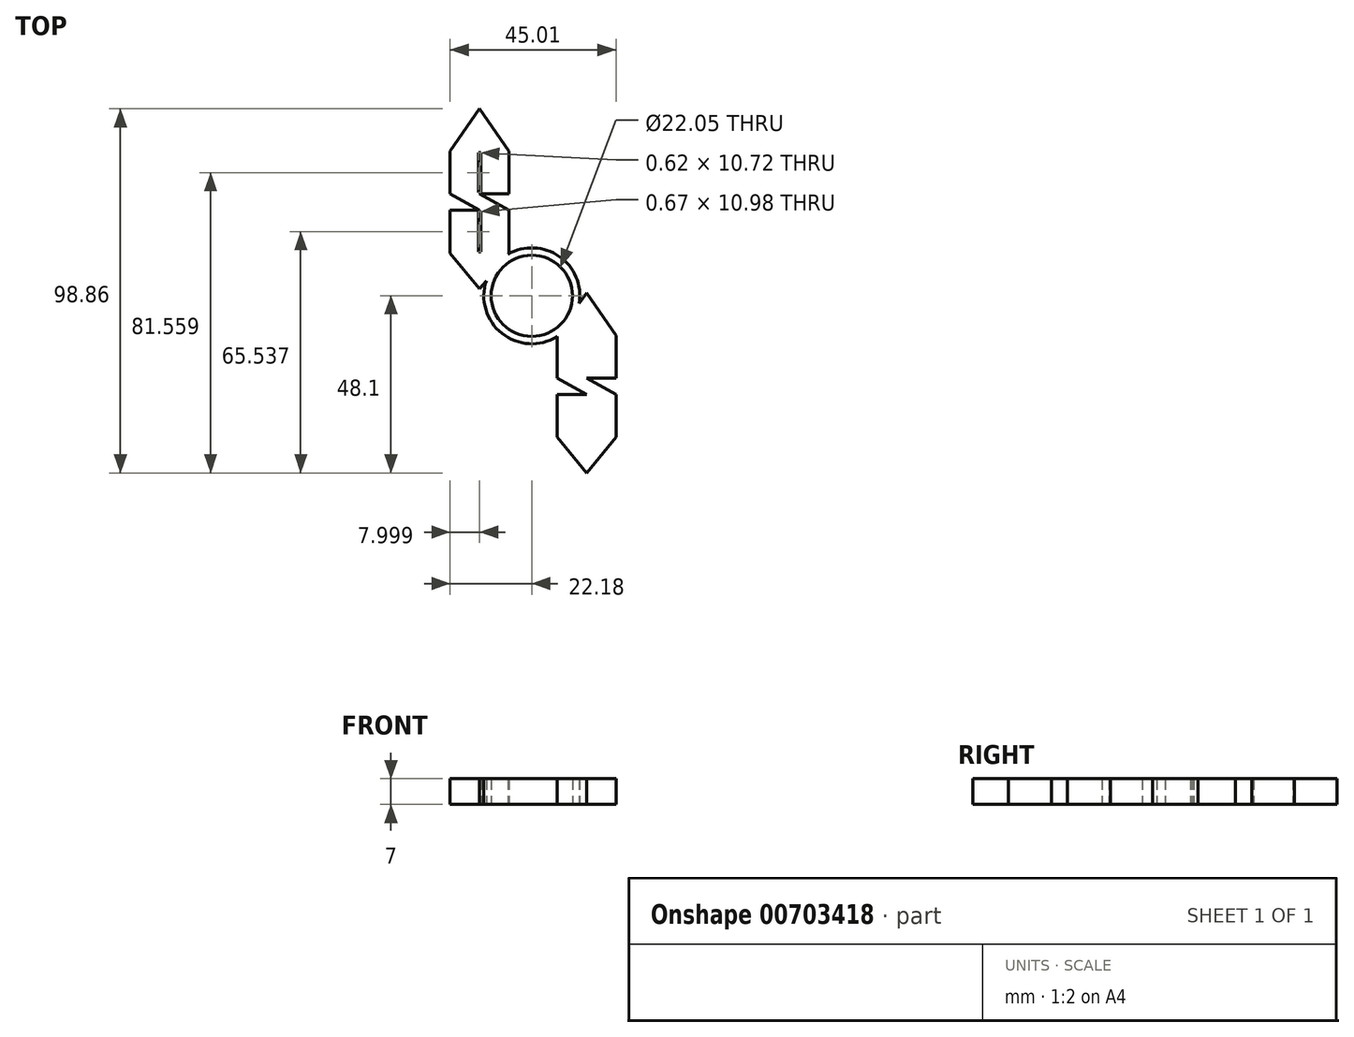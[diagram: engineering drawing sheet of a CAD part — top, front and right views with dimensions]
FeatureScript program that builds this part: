
annotation { "Feature Type Name" : "Feature", "Feature Type Description" : "" }
export const myFeature = defineFeature(function(context is Context, id is Id, definition is map)
    precondition{}
    {
        {
            var Q0;
            Q0=qCreatedBy(makeId("Top.planeOp"),FACE);
            var sketch = newSketch(context, id + "F0", { "sketchPlane" : qUnion([Q0])});
            skCircle(sketch, "E0", {"center": v(0, 0) * mm, "radius": 11.03 * mm});
            skCircle(sketch, "E1.0", {"center": v(0, 0) * mm, "radius": 13.02 * mm});
            skLineSegment(sketch, "E2", {"start": v(-6.18, 11.63) * mm, "end": v(-6.18, 23.25) * mm});
            skLineSegment(sketch, "E3", {"start": v(-14.18, 11.63) * mm, "end": v(-14.18, 23.25) * mm});
            skLineSegment(sketch, "E4", {"start": v(-22.18, 23.25) * mm, "end": v(-22.18, 11.63) * mm});
            skLineSegment(sketch, "E5", {"start": v(-6.18, 27.65) * mm, "end": v(-6.18, 39.27) * mm});
            skLineSegment(sketch, "E6", {"start": v(-14.18, 27.65) * mm, "end": v(-14.18, 39.27) * mm});
            skLineSegment(sketch, "E7", {"start": v(-22.18, 39.27) * mm, "end": v(-22.18, 27.65) * mm});
            skLineSegment(sketch, "E8", {"start": v(-6.18, 39.27) * mm, "end": v(-14.18, 50.76) * mm});
            skLineSegment(sketch, "E9", {"start": v(-14.18, 50.76) * mm, "end": v(-22.18, 39.27) * mm});
            skLineSegment(sketch, "E10", {"start": v(-14.18, 27.65) * mm, "end": v(-6.18, 27.65) * mm});
            skLineSegment(sketch, "E11", {"start": v(-14.18, 27.65) * mm, "end": v(-6.18, 23.25) * mm});
            skLineSegment(sketch, "E12", {"start": v(-22.18, 27.65) * mm, "end": v(-14.18, 23.25) * mm});
            skLineSegment(sketch, "E13", {"start": v(-14.18, 23.25) * mm, "end": v(-22.18, 23.25) * mm});
            skLineSegment(sketch, "E14", {"start": v(-22.18, 11.63) * mm, "end": v(-14.18, 1.9) * mm});
            skLineSegment(sketch, "E15", {"start": v(-14.18, 1.9) * mm, "end": v(-6.18, 11.63) * mm});
            skLineSegment(sketch, "E16.bottom", {"start": v(-13.87, 38.82) * mm, "end": v(-14.5, 38.82) * mm});
            skLineSegment(sketch, "E16.top", {"start": v(-13.87, 28.1) * mm, "end": v(-14.5, 28.1) * mm});
            skLineSegment(sketch, "E16.left", {"start": v(-13.87, 38.82) * mm, "end": v(-13.87, 28.1) * mm});
            skLineSegment(sketch, "E16.right", {"start": v(-14.5, 38.82) * mm, "end": v(-14.5, 28.1) * mm});
            skPoint(sketch, "E16.middle", {"position": v(-14.18, 33.46) * mm});
            skLineSegment(sketch, "E17.bottom", {"start": v(-13.85, 22.93) * mm, "end": v(-14.52, 22.93) * mm});
            skLineSegment(sketch, "E17.top", {"start": v(-13.85, 11.95) * mm, "end": v(-14.52, 11.95) * mm});
            skLineSegment(sketch, "E17.left", {"start": v(-13.85, 22.93) * mm, "end": v(-13.85, 11.95) * mm});
            skLineSegment(sketch, "E17.right", {"start": v(-14.52, 22.93) * mm, "end": v(-14.52, 11.95) * mm});
            skPoint(sketch, "E17.middle", {"position": v(-14.18, 17.44) * mm});
            skLineSegment(sketch, "E18", {"start": v(22.83, -38.38) * mm, "end": v(22.83, -26.76) * mm});
            skLineSegment(sketch, "E19", {"start": v(14.83, -38.38) * mm, "end": v(14.83, -26.76) * mm});
            skLineSegment(sketch, "E20", {"start": v(6.83, -26.76) * mm, "end": v(6.83, -38.38) * mm});
            skLineSegment(sketch, "E21", {"start": v(22.83, -22.36) * mm, "end": v(22.83, -10.73) * mm});
            skLineSegment(sketch, "E22", {"start": v(14.83, -22.36) * mm, "end": v(14.83, -10.73) * mm});
            skLineSegment(sketch, "E23", {"start": v(6.83, -10.73) * mm, "end": v(6.83, -22.36) * mm});
            skLineSegment(sketch, "E24", {"start": v(22.83, -10.73) * mm, "end": v(14.83, 0.76) * mm});
            skLineSegment(sketch, "E25", {"start": v(14.83, 0.76) * mm, "end": v(6.83, -10.73) * mm});
            skLineSegment(sketch, "E26", {"start": v(14.83, -22.36) * mm, "end": v(22.83, -22.36) * mm});
            skLineSegment(sketch, "E27", {"start": v(14.83, -22.36) * mm, "end": v(22.83, -26.76) * mm});
            skLineSegment(sketch, "E28", {"start": v(6.83, -22.36) * mm, "end": v(14.83, -26.76) * mm});
            skLineSegment(sketch, "E29", {"start": v(14.83, -26.76) * mm, "end": v(6.83, -26.76) * mm});
            skLineSegment(sketch, "E30", {"start": v(6.83, -38.38) * mm, "end": v(14.83, -48.1) * mm});
            skLineSegment(sketch, "E31", {"start": v(14.83, -48.1) * mm, "end": v(22.83, -38.38) * mm});
            skSolve(sketch);
        }
        {
            var Q0;
            Q0 = qSketchRegion(id + "F0", true);
            extrude(context, id + "F1", {"entities" : qUnion([Q0]), "depth" : 7 * mm, "offsetDistance" : 25 * mm});
        }
    });
